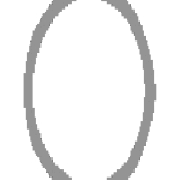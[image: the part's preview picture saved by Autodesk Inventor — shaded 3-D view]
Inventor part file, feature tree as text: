
AUTODESK INVENTOR PART (.ipt)
format: ipt  version: 2021 (Build 250183000, 183)  size: 112,640 bytes
history: native  units: in
note: dims shown in document units (in); Inventor stores cm internally (conversion verified against a paired STEP export)
features: other x4, sketch x3, plane x1
ambient origin geometry x8: Origin, YZ Plane, XZ Plane, XY Plane, X Axis, Y Axis, Z Axis, Center Point
bodies: Solid1 (feature_tree), Body (feature_tree)
feature tree (8):
  other  "Driven Length"
  other  "Frame Generator"
  other  "Start Plane"
  other  "End Plane"
  sketch  "Sketch"  dims[d2=13.2634in d4=-0.0in d5=13.2634in d6=0.12in d7=0.0in d8=90.0deg d9=13.2634in]
  sketch  "Sketch2"  dims[d0=1.0in]
  plane  "Work Plane3"
  sketch  "Sketch3"  dims[d1=0.065in]
